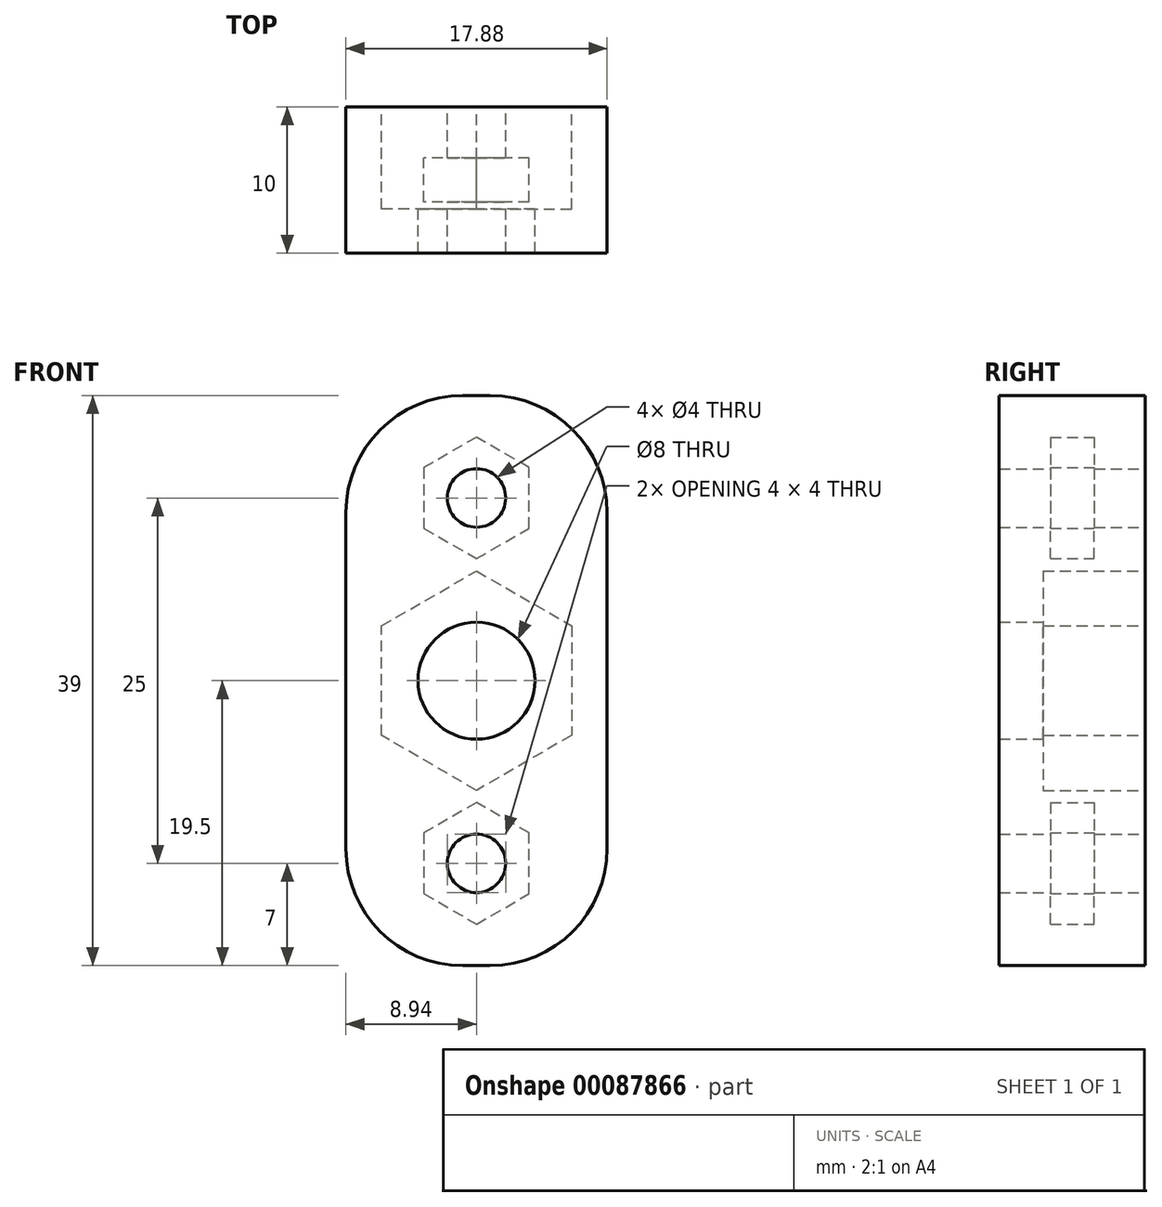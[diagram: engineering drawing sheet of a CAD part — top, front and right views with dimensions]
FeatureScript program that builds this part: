
annotation { "Feature Type Name" : "Feature", "Feature Type Description" : "" }
export const myFeature = defineFeature(function(context is Context, id is Id, definition is map)
    precondition{}
    {
        {
            var Q0;
            Q0=qCreatedBy(makeId("Front.planeOp"),FACE);
            var sketch = newSketch(context, id + "F0", { "sketchPlane" : qUnion([Q0])});
            skCircle(sketch, "E0.cCircle", {"center": v(0, 0) * mm, "radius": 6.5 * mm, "construction": true});
            skLineSegment(sketch, "E0.0", {"start": v(6.5, 3.75) * mm, "end": v(6.5, -3.75) * mm});
            skLineSegment(sketch, "E0.1", {"start": v(6.5, -3.75) * mm, "end": v(0, -7.5) * mm});
            skLineSegment(sketch, "E0.2", {"start": v(0, -7.5) * mm, "end": v(-6.5, -3.75) * mm});
            skLineSegment(sketch, "E0.3", {"start": v(-6.5, -3.75) * mm, "end": v(-6.5, 3.75) * mm});
            skLineSegment(sketch, "E0.4", {"start": v(-6.5, 3.75) * mm, "end": v(0, 7.5) * mm});
            skLineSegment(sketch, "E0.5", {"start": v(0, 7.5) * mm, "end": v(6.5, 3.75) * mm});
            skPoint(sketch, "E0.0.midPoint", {"position": v(6.5, 0) * mm});
            skLineSegment(sketch, "E1.bottom", {"start": v(8.94, -19.5) * mm, "end": v(-8.94, -19.5) * mm});
            skLineSegment(sketch, "E1.top", {"start": v(8.94, 19.5) * mm, "end": v(-8.94, 19.5) * mm});
            skLineSegment(sketch, "E1.left", {"start": v(8.94, -19.5) * mm, "end": v(8.94, 19.5) * mm});
            skLineSegment(sketch, "E1.right", {"start": v(-8.94, -19.5) * mm, "end": v(-8.94, 19.5) * mm});
            skCircle(sketch, "E2", {"center": v(0, 12.5) * mm, "radius": 2 * mm});
            skCircle(sketch, "E3", {"center": v(0, -12.5) * mm, "radius": 2 * mm});
            skSolve(sketch);
        }
        {
            var Q0;
            Q0 = qSketchRegion(id + "F0", true);
            extrude(context, id + "F1", {"entities" : qUnion([Q0]), "depth" : 7 * mm});
        }
        {
            var Q0;
            Q0=makeQuery(id+"F1.opExtrude","CAP_FACE",FACE,{"disambiguationData":[OSD([sQuery(id+"F0.wireOp",EDGE,"E0.0"),sQuery(id+"F0.wireOp",EDGE,"E0.1"),sQuery(id+"F0.wireOp",EDGE,"E0.2"),sQuery(id+"F0.wireOp",EDGE,"E0.3"),sQuery(id+"F0.wireOp",EDGE,"E0.4"),sQuery(id+"F0.wireOp",EDGE,"E0.5"),sQuery(id+"F0.wireOp",EDGE,"E1.bottom"),sQuery(id+"F0.wireOp",EDGE,"E1.top"),sQuery(id+"F0.wireOp",EDGE,"E1.left"),sQuery(id+"F0.wireOp",EDGE,"E1.right"),sQuery(id+"F0.wireOp",EDGE,"E2"),sQuery(id+"F0.wireOp",EDGE,"E3")])],"isStart":false});
            var sketch = newSketch(context, id + "F2", { "sketchPlane" : qUnion([Q0])});
            skCircle(sketch, "E4", {"center": v(0, 0) * mm, "radius": 4 * mm});
            skSolve(sketch);
        }
        {
            var Q0;
            Q0=makeQuery(id+"F2.imprint","IMPRINT",FACE,{"disambiguationData":[TD([[makeQuery(id+"F2.imprint","IMPRINT",EDGE,{"derivedFrom":makeQuery(id+"F1.opExtrude","CAP_EDGE",EDGE,{"disambiguationData":[OSD([sQuery(id+"F0.wireOp",EDGE,"E0.0")])],"isStart":false})}),1.0]])]});
            var Q1;
            Q1=makeQuery(id+"F2.imprint","IMPRINT",FACE,{"disambiguationData":[TD([[makeQuery(id+"F2.imprint","IMPRINT",EDGE,{"derivedFrom":sQuery(id+"F2.wireOp",EDGE,"E4")}),-1.0]])]});
            extrude(context, id + "F3", {"entities" : qUnion([Q0, Q1]), "operationType" : NewBodyOperationType.ADD, "depth" : 3 * mm});
        }
        {
            var Q0;
            Q0=makeQuery(id+"F1.opExtrude","CAP_FACE",FACE,{"disambiguationData":[OSD([sQuery(id+"F0.wireOp",EDGE,"E0.0"),sQuery(id+"F0.wireOp",EDGE,"E0.1"),sQuery(id+"F0.wireOp",EDGE,"E0.2"),sQuery(id+"F0.wireOp",EDGE,"E0.3"),sQuery(id+"F0.wireOp",EDGE,"E0.4"),sQuery(id+"F0.wireOp",EDGE,"E0.5"),sQuery(id+"F0.wireOp",EDGE,"E1.bottom"),sQuery(id+"F0.wireOp",EDGE,"E1.top"),sQuery(id+"F0.wireOp",EDGE,"E1.left"),sQuery(id+"F0.wireOp",EDGE,"E1.right"),sQuery(id+"F0.wireOp",EDGE,"E2"),sQuery(id+"F0.wireOp",EDGE,"E3")])],"isStart":true});
            cPlane(context, id + "F4", {"entities" : qUnion([Q0]), "cplaneType" : CPlaneType.OFFSET, "offset" : 5 * mm, "oppositeDirection" : true, "width" : 150 * mm, "height" : 150 * mm});
        }
        {
            var Q0;
            Q0=qCreatedBy(id+"F4.planeOp",FACE);
            var sketch = newSketch(context, id + "F5", { "sketchPlane" : qUnion([Q0])});
            skCircle(sketch, "E5.0", {"center": v(0, -12.5) * mm, "radius": 2 * mm, "construction": true});
            skCircle(sketch, "E6.0", {"center": v(0, 12.5) * mm, "radius": 2 * mm, "construction": true});
            skCircle(sketch, "E7.cCircle", {"center": v(0, -12.5) * mm, "radius": 3.6 * mm, "construction": true});
            skLineSegment(sketch, "E7.0", {"start": v(3.6, -10.42) * mm, "end": v(3.6, -14.58) * mm});
            skLineSegment(sketch, "E7.1", {"start": v(3.6, -14.58) * mm, "end": v(0, -16.66) * mm});
            skLineSegment(sketch, "E7.2", {"start": v(0, -16.66) * mm, "end": v(-3.6, -14.58) * mm});
            skLineSegment(sketch, "E7.3", {"start": v(-3.6, -14.58) * mm, "end": v(-3.6, -10.42) * mm});
            skLineSegment(sketch, "E7.4", {"start": v(-3.6, -10.42) * mm, "end": v(0, -8.34) * mm});
            skLineSegment(sketch, "E7.5", {"start": v(0, -8.34) * mm, "end": v(3.6, -10.42) * mm});
            skPoint(sketch, "E7.0.midPoint", {"position": v(3.6, -12.5) * mm});
            skCircle(sketch, "E8.cCircle", {"center": v(0, 12.5) * mm, "radius": 3.6 * mm, "construction": true});
            skLineSegment(sketch, "E8.0", {"start": v(3.6, 14.58) * mm, "end": v(3.6, 10.42) * mm});
            skLineSegment(sketch, "E8.1", {"start": v(3.6, 10.42) * mm, "end": v(0, 8.34) * mm});
            skLineSegment(sketch, "E8.2", {"start": v(0, 8.34) * mm, "end": v(-3.6, 10.42) * mm});
            skLineSegment(sketch, "E8.3", {"start": v(-3.6, 10.42) * mm, "end": v(-3.6, 14.58) * mm});
            skLineSegment(sketch, "E8.4", {"start": v(-3.6, 14.58) * mm, "end": v(0, 16.66) * mm});
            skLineSegment(sketch, "E8.5", {"start": v(0, 16.66) * mm, "end": v(3.6, 14.58) * mm});
            skPoint(sketch, "E8.0.midPoint", {"position": v(3.6, 12.5) * mm});
            skSolve(sketch);
        }
        {
            var Q0;
            Q0 = qSketchRegion(id + "F5", true);
            extrude(context, id + "F6", {"entities" : qUnion([Q0]), "operationType" : NewBodyOperationType.REMOVE, "endBound" : BoundingType.SYMMETRIC, "oppositeDirection" : true, "depth" : 3 * mm});
        }
        {
            var Q0;
            {var subQ0=sQuery(id+"F0.wireOp",EDGE,"E1.right");var subQ1=sQuery(id+"F0.wireOp",EDGE,"E1.bottom");Q0=makeQuery(id+"F3.boolean.opBoolean","MERGE",EDGE,{"derivedFrom":[makeQuery(id+"F1.opExtrude","SWEPT_EDGE",EDGE,{"disambiguationData":[OSD([subQ1,subQ0])]}),makeQuery(id+"F3.opExtrude","SWEPT_EDGE",EDGE,{"disambiguationData":[OSD([subQ1,subQ0])]})]});}
            var Q1;
            {var subQ0=sQuery(id+"F0.wireOp",EDGE,"E1.left");var subQ1=sQuery(id+"F0.wireOp",EDGE,"E1.bottom");Q1=makeQuery(id+"F3.boolean.opBoolean","MERGE",EDGE,{"derivedFrom":[makeQuery(id+"F1.opExtrude","SWEPT_EDGE",EDGE,{"disambiguationData":[OSD([subQ1,subQ0])]}),makeQuery(id+"F3.opExtrude","SWEPT_EDGE",EDGE,{"disambiguationData":[OSD([subQ1,subQ0])]})]});}
            var Q2;
            {var subQ0=sQuery(id+"F0.wireOp",EDGE,"E1.right");var subQ1=sQuery(id+"F0.wireOp",EDGE,"E1.top");Q2=makeQuery(id+"F3.boolean.opBoolean","MERGE",EDGE,{"derivedFrom":[makeQuery(id+"F1.opExtrude","SWEPT_EDGE",EDGE,{"disambiguationData":[OSD([subQ1,subQ0])]}),makeQuery(id+"F3.opExtrude","SWEPT_EDGE",EDGE,{"disambiguationData":[OSD([subQ1,subQ0])]})]});}
            var Q3;
            {var subQ0=sQuery(id+"F0.wireOp",EDGE,"E1.left");var subQ1=sQuery(id+"F0.wireOp",EDGE,"E1.top");Q3=makeQuery(id+"F3.boolean.opBoolean","MERGE",EDGE,{"derivedFrom":[makeQuery(id+"F1.opExtrude","SWEPT_EDGE",EDGE,{"disambiguationData":[OSD([subQ1,subQ0])]}),makeQuery(id+"F3.opExtrude","SWEPT_EDGE",EDGE,{"disambiguationData":[OSD([subQ1,subQ0])]})]});}
            fillet(context, id + "F7", {"entities" : qUnion([Q0, Q1, Q2, Q3]), "radius" : 8 * mm, "tangentPropagation" : true, "allowEdgeOverflow" : false});
        }
    });
